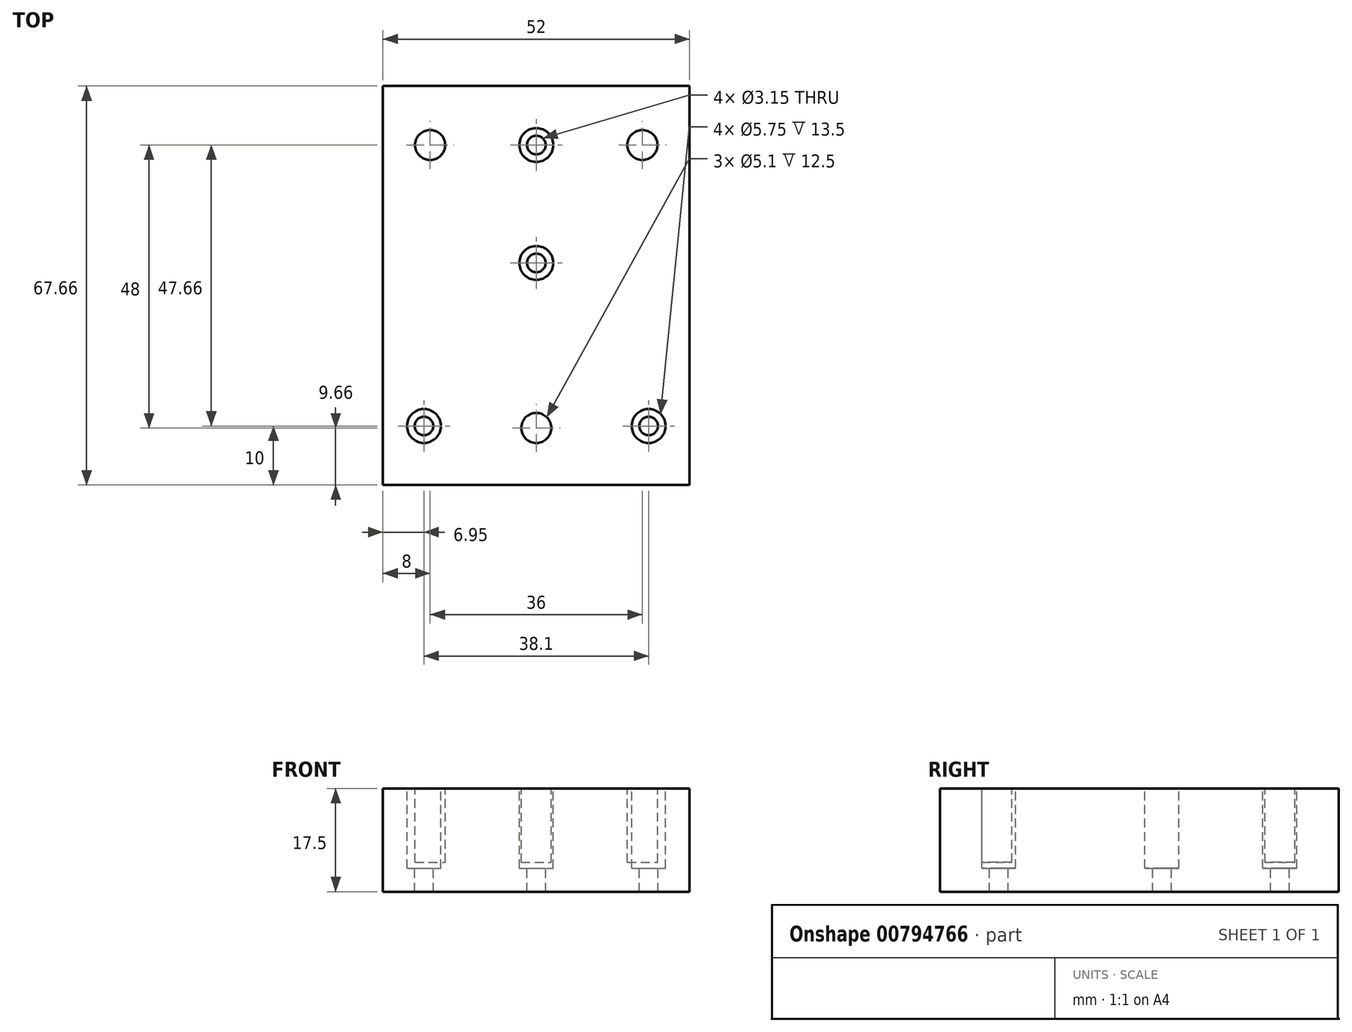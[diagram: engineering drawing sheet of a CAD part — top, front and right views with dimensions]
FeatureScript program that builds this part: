
annotation { "Feature Type Name" : "Feature", "Feature Type Description" : "" }
export const myFeature = defineFeature(function(context is Context, id is Id, definition is map)
    precondition{}
    {
        {
            var Q0;
            Q0=qCreatedBy(makeId("Top.planeOp"),FACE);
            var sketch = newSketch(context, id + "F0", { "sketchPlane" : qUnion([Q0])});
            skCircle(sketch, "E0", {"center": v(0, 0) * mm, "radius": 1.57 * mm});
            skCircle(sketch, "E1", {"center": v(0, -20) * mm, "radius": 1.57 * mm});
            skCircle(sketch, "E2", {"center": v(-19.05, 27.66) * mm, "radius": 1.58 * mm});
            skCircle(sketch, "E3", {"center": v(19.05, 27.66) * mm, "radius": 1.57 * mm});
            skSolve(sketch);
        }
        {
            var Q0;
            Q0=qCreatedBy(makeId("Top.planeOp"),FACE);
            var sketch = newSketch(context, id + "F1", { "sketchPlane" : qUnion([Q0])});
            skLineSegment(sketch, "E4.bottom", {"start": v(-26, -30) * mm, "end": v(26, -30) * mm});
            skLineSegment(sketch, "E4.top", {"start": v(-26, 37.66) * mm, "end": v(26, 37.66) * mm});
            skLineSegment(sketch, "E4.left", {"start": v(-26, -30) * mm, "end": v(-26, 37.66) * mm});
            skLineSegment(sketch, "E4.right", {"start": v(26, -30) * mm, "end": v(26, 37.66) * mm});
            skSolve(sketch);
        }
        {
            var Q0;
            Q0=qSketchRegion(id+"F1",true);
            extrude(context, id + "F2", {"entities" : qUnion([Q0]), "depth" : 17.5 * mm, "offsetDistance" : 25 * mm});
        }
        {
            var Q0;
            Q0=qSketchRegion(id+"F0",true);
            extrude(context, id + "F3", {"entities" : qUnion([Q0]), "operationType" : NewBodyOperationType.REMOVE, "oppositeDirection" : true, "depth" : -17.5 * mm, "offsetDistance" : 25 * mm});
        }
        {
            var Q0;
            Q0=makeQuery(id+"F2.opExtrude","CAP_FACE",FACE,{"disambiguationData":[OSD([sQuery(id+"F1.wireOp",EDGE,"E4.bottom"),sQuery(id+"F1.wireOp",EDGE,"E4.top"),sQuery(id+"F1.wireOp",EDGE,"E4.left"),sQuery(id+"F1.wireOp",EDGE,"E4.right")])],"isStart":true});
            var sketch = newSketch(context, id + "F4", { "sketchPlane" : qUnion([Q0])});
            skCircle(sketch, "E5", {"center": v(0, 0) * mm, "radius": 2.88 * mm});
            skCircle(sketch, "E6", {"center": v(19.05, -27.66) * mm, "radius": 2.88 * mm});
            skCircle(sketch, "E7", {"center": v(-19.05, -27.66) * mm, "radius": 2.88 * mm});
            skCircle(sketch, "E8", {"center": v(0, 20) * mm, "radius": 2.88 * mm});
            skSolve(sketch);
        }
        {
            var Q0;
            Q0=qSketchRegion(id+"F4",true);
            extrude(context, id + "F5", {"entities" : qUnion([Q0]), "operationType" : NewBodyOperationType.REMOVE, "oppositeDirection" : true, "depth" : 13.5 * mm, "offsetDistance" : 25 * mm});
        }
        {
            var Q0;
            Q0=makeQuery(id+"F2.opExtrude","CAP_FACE",FACE,{"disambiguationData":[OSD([sQuery(id+"F1.wireOp",EDGE,"E4.bottom"),sQuery(id+"F1.wireOp",EDGE,"E4.top"),sQuery(id+"F1.wireOp",EDGE,"E4.left"),sQuery(id+"F1.wireOp",EDGE,"E4.right")])],"isStart":true});
            var sketch = newSketch(context, id + "F6", { "sketchPlane" : qUnion([Q0])});
            skCircle(sketch, "E9", {"center": v(0, -28) * mm, "radius": 2.55 * mm});
            skCircle(sketch, "E10", {"center": v(-18, 20) * mm, "radius": 2.55 * mm});
            skCircle(sketch, "E11", {"center": v(18, 20) * mm, "radius": 2.55 * mm});
            skSolve(sketch);
        }
        {
            var Q0;
            Q0=qSketchRegion(id+"F6",true);
            extrude(context, id + "F7", {"entities" : qUnion([Q0]), "operationType" : NewBodyOperationType.REMOVE, "oppositeDirection" : true, "depth" : 12.5 * mm, "offsetDistance" : 25 * mm});
        }
        {
            var Q0;
            Q0=makeQuery(id+"F2.opExtrude","SWEPT_BODY",BODY,{"disambiguationData":[OSD([sQuery(id+"F1.wireOp",EDGE,"E4.bottom"),sQuery(id+"F1.wireOp",EDGE,"E4.top"),sQuery(id+"F1.wireOp",EDGE,"E4.left"),sQuery(id+"F1.wireOp",EDGE,"E4.right")])]});
            var Q1;
            Q1=makeQuery(id+"F2.opExtrude","CAP_EDGE",EDGE,{"disambiguationData":[OSD([sQuery(id+"F1.wireOp",EDGE,"E4.top")])],"isStart":false});
            var Q2;
            Q2=makeQuery(id+"F2.opExtrude","CAP_EDGE",EDGE,{"disambiguationData":[OSD([sQuery(id+"F1.wireOp",EDGE,"E4.left")])],"isStart":false});
            transform(context, id + "F8", {"entities" : qUnion([Q0]), "transformType" : TransformType.ROTATION, "transformAxis" : qUnion([Q2]), "angle" : 180 * degree, "makeCopy" : false});
        }
        {
            var Q0;
            Q0=makeQuery(id+"F2.opExtrude","SWEPT_BODY",BODY,{"disambiguationData":[OSD([sQuery(id+"F1.wireOp",EDGE,"E4.bottom"),sQuery(id+"F1.wireOp",EDGE,"E4.top"),sQuery(id+"F1.wireOp",EDGE,"E4.left"),sQuery(id+"F1.wireOp",EDGE,"E4.right")])]});
            var Q1;
            Q1=makeQuery(id+"F2.opExtrude","SWEPT_EDGE",EDGE,{"disambiguationData":[OSD([sQuery(id+"F1.wireOp",EDGE,"E4.top"),sQuery(id+"F1.wireOp",EDGE,"E4.left")])]});
            transform(context, id + "F9", {"entities" : qUnion([Q0]), "transformType" : TransformType.ROTATION, "transformAxis" : qUnion([Q1]), "angle" : 180 * degree, "makeCopy" : false});
        }
        {
            var Q0;
            Q0=makeQuery(id+"F2.opExtrude","CAP_EDGE",EDGE,{"disambiguationData":[OSD([sQuery(id+"F1.wireOp",EDGE,"E4.bottom")])],"isStart":true});
            cPoint(context, id + "F10", {"entities" : qUnion([Q0]), "parameter" : 0.5});
        }
        {
            var Q0;
            Q0=makeQuery(id+"F2.opExtrude","SWEPT_BODY",BODY,{"disambiguationData":[OSD([sQuery(id+"F1.wireOp",EDGE,"E4.bottom"),sQuery(id+"F1.wireOp",EDGE,"E4.top"),sQuery(id+"F1.wireOp",EDGE,"E4.left"),sQuery(id+"F1.wireOp",EDGE,"E4.right")])]});
            var Q1;
            Q1=qCreatedBy(makeId("Origin.pointOp"),VERTEX);
            var Q2;
            Q2=qCreatedBy(id+"F10",VERTEX);
            transform(context, id + "F11", {"entities" : qUnion([Q0]), "transformType" : TransformType.TRANSLATION_ENTITY, "oppositeDirectionEntity" : true, "transformLine" : qUnion([Q1, Q2]), "makeCopy" : false});
        }
    });
